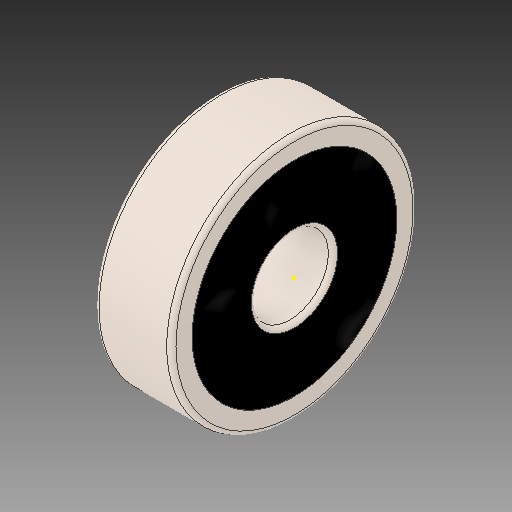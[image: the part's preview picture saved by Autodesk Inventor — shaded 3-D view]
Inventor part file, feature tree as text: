
AUTODESK INVENTOR PART (.ipt)
format: ipt  version: 2018 (Build 220112000, 112)  size: 2,315,264 bytes
history: imported  units: mm
features: other x22, sketch x3, imported_body x1
ambient origin geometry x8: Origin, YZ Plane, XZ Plane, XY Plane, X Axis, Y Axis, Z Axis, Center Point
bodies: Solid1 (imported_parasolid), Solid2 (imported_parasolid), Solid3 (imported_parasolid), Solid4 (imported_parasolid), Solid5 (imported_parasolid), Solid6 (imported_parasolid), Solid7 (imported_parasolid), Solid8 (imported_parasolid), Solid9 (imported_parasolid), Solid10 (imported_parasolid), Solid11 (imported_parasolid), Solid12 (imported_parasolid), Solid13 (imported_parasolid), Solid14 (imported_parasolid), Solid15 (imported_parasolid), Solid16 (imported_parasolid), Solid17 (imported_parasolid), Solid18 (imported_parasolid), Solid19 (imported_parasolid), Solid20 (imported_parasolid)
feature tree (26):
  other  "SKF 625_MIR1.ipt"
  other  "Solid1::SKF 625_MIR1.ipt"
  other  "Solid2::SKF 625_MIR1.ipt"
  other  "Solid3::SKF 625_MIR1.ipt"
  other  "Solid4::SKF 625_MIR1.ipt"
  other  "Solid5::SKF 625_MIR1.ipt"
  other  "Solid6::SKF 625_MIR1.ipt"
  other  "Solid7::SKF 625_MIR1.ipt"
  other  "Solid8::SKF 625_MIR1.ipt"
  other  "Solid9::SKF 625_MIR1.ipt"
  other  "Solid10::SKF 625_MIR1.ipt"
  other  "Solid11::SKF 625_MIR1.ipt"
  other  "Solid12::SKF 625_MIR1.ipt"
  other  "Solid13::SKF 625_MIR1.ipt"
  other  "Solid14::SKF 625_MIR1.ipt"
  other  "Solid15::SKF 625_MIR1.ipt"
  other  "Solid16::SKF 625_MIR1.ipt"
  other  "Solid17::SKF 625_MIR1.ipt"
  other  "Solid18::SKF 625_MIR1.ipt"
  other  "Solid19::SKF 625_MIR1.ipt"
  other  "Solid20::SKF 625_MIR1.ipt"
  other  "TaggingFeature1"
  sketch  "Sketch1"  dims[d0=10.0mm]
  sketch  "Sketch2"
  sketch  "Sketch3"
  imported_body  NMx_Import_Brep_tag  [imported B-rep: ~49 faces, bbox_mm=None]
